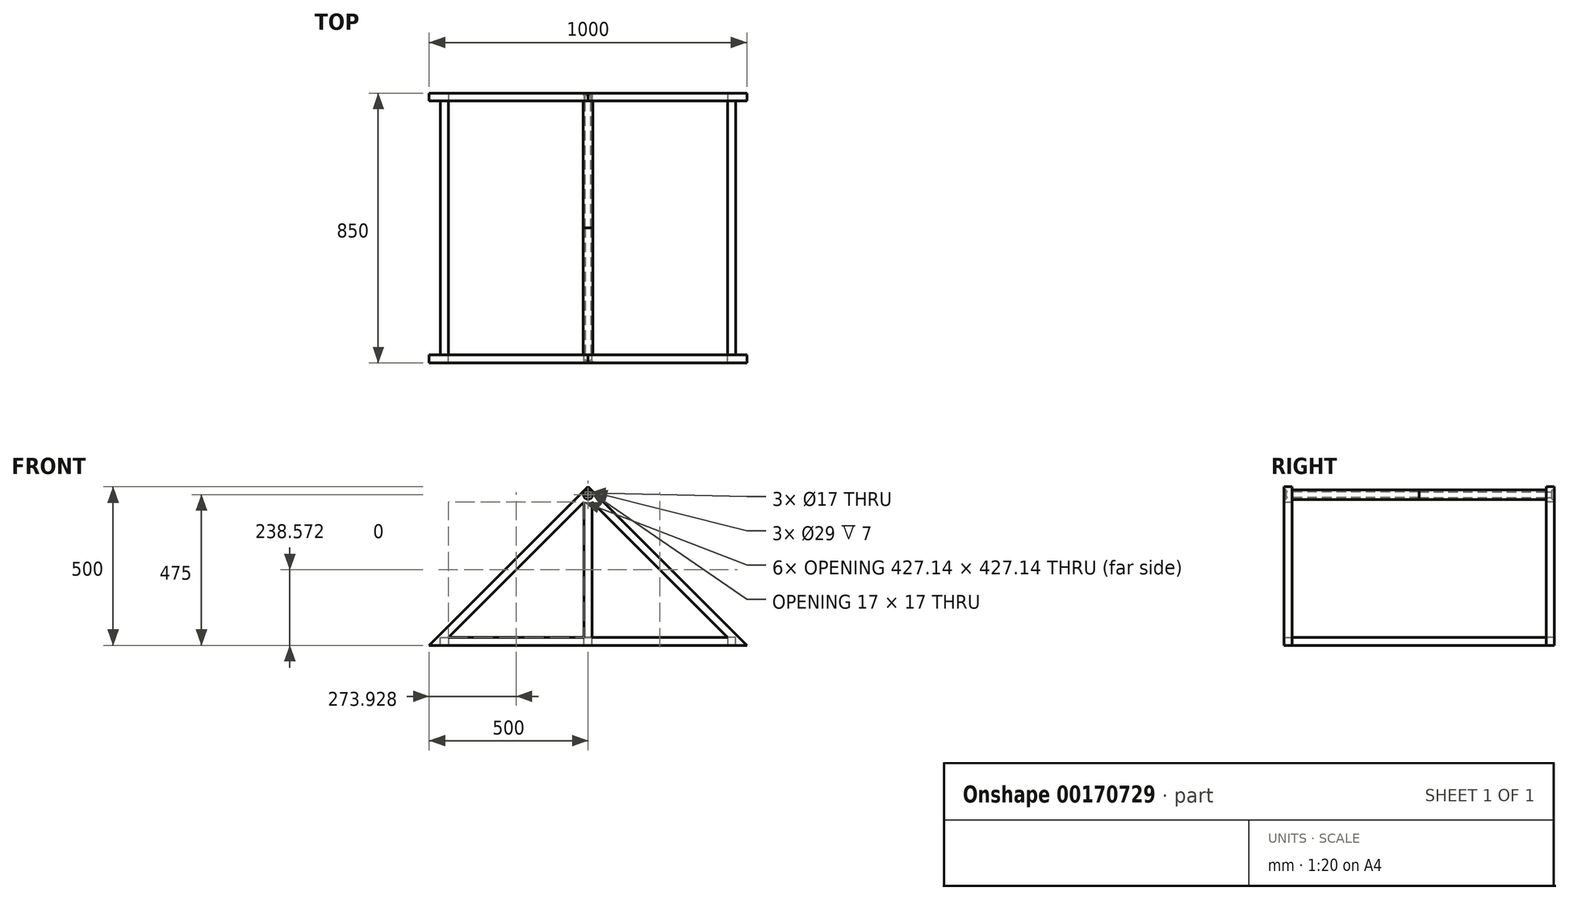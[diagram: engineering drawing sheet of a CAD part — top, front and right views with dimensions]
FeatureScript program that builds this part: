
annotation { "Feature Type Name" : "Feature", "Feature Type Description" : "" }
export const myFeature = defineFeature(function(context is Context, id is Id, definition is map)
    precondition{}
    {
        {
            var Q0;
            Q0=qCreatedBy(makeId("Front.planeOp"),FACE);
            var sketch = newSketch(context, id + "F0", { "sketchPlane" : qUnion([Q0])});
            skLineSegment(sketch, "E0", {"start": v(0, -500) * mm, "end": v(500, -500) * mm});
            skLineSegment(sketch, "E1", {"start": v(0, -500) * mm, "end": v(-500, -500) * mm});
            skLineSegment(sketch, "E2", {"start": v(0, 0) * mm, "end": v(-500, -500) * mm});
            skLineSegment(sketch, "E3", {"start": v(0, 0) * mm, "end": v(500, -500) * mm});
            skLineSegment(sketch, "E4.0", {"start": v(-12.5, -475) * mm, "end": v(-439.64, -475) * mm});
            skLineSegment(sketch, "E4.1", {"start": v(12.5, -475) * mm, "end": v(439.64, -475) * mm});
            skLineSegment(sketch, "E5.trimOffspring", {"start": v(12.5, -47.86) * mm, "end": v(12.5, -475) * mm});
            skLineSegment(sketch, "E6.trimOffspring", {"start": v(-12.5, -47.86) * mm, "end": v(-439.64, -475) * mm});
            skLineSegment(sketch, "E7.trimOffspring", {"start": v(12.5, -47.86) * mm, "end": v(439.64, -475) * mm});
            skLineSegment(sketch, "E8.trimOffspring", {"start": v(-12.5, -47.86) * mm, "end": v(-12.5, -475) * mm});
            skSolve(sketch);
        }
        {
            var Q0;
            Q0=makeQuery(id+"F0.imprint","IMPRINT",FACE,{"disambiguationData":[TD([[makeQuery(id+"F0.imprint","IMPRINT",EDGE,{"derivedFrom":sQuery(id+"F0.wireOp",EDGE,"E0")}),1.0]])]});
            extrude(context, id + "F1", {"entities" : qUnion([Q0]), "depth" : 25 * mm});
        }
        {
            var Q0;
            Q0=qCreatedBy(makeId("Front.planeOp"),FACE);
            cPlane(context, id + "F2", {"entities" : qUnion([Q0]), "cplaneType" : CPlaneType.OFFSET, "offset" : 400 * mm, "oppositeDirection" : true, "width" : 150 * mm, "height" : 150 * mm});
        }
        {
            var Q0;
            Q0=makeQuery(id+"F1.opExtrude","SWEPT_BODY",BODY,{"disambiguationData":[OSD([sQuery(id+"F0.wireOp",EDGE,"E0"),sQuery(id+"F0.wireOp",EDGE,"E1"),sQuery(id+"F0.wireOp",EDGE,"E2"),sQuery(id+"F0.wireOp",EDGE,"E3"),sQuery(id+"F0.wireOp",EDGE,"E4.0"),sQuery(id+"F0.wireOp",EDGE,"E4.1"),sQuery(id+"F0.wireOp",EDGE,"E5.trimOffspring"),sQuery(id+"F0.wireOp",EDGE,"E6.trimOffspring"),sQuery(id+"F0.wireOp",EDGE,"E7.trimOffspring"),sQuery(id+"F0.wireOp",EDGE,"E8.trimOffspring")])]});
            var Q1;
            Q1=qCreatedBy(id+"F2.planeOp",FACE);
            mirror(context, id + "F3", {"entities" : qUnion([Q0]), "mirrorPlane" : qUnion([Q1])});
        }
        {
            var Q0;
            Q0=makeQuery(id+"F1.opExtrude","CAP_FACE",FACE,{"disambiguationData":[OSD([sQuery(id+"F0.wireOp",EDGE,"E0"),sQuery(id+"F0.wireOp",EDGE,"E1"),sQuery(id+"F0.wireOp",EDGE,"E2"),sQuery(id+"F0.wireOp",EDGE,"E3"),sQuery(id+"F0.wireOp",EDGE,"E4.0"),sQuery(id+"F0.wireOp",EDGE,"E4.1"),sQuery(id+"F0.wireOp",EDGE,"E5.trimOffspring"),sQuery(id+"F0.wireOp",EDGE,"E6.trimOffspring"),sQuery(id+"F0.wireOp",EDGE,"E7.trimOffspring"),sQuery(id+"F0.wireOp",EDGE,"E8.trimOffspring")])],"isStart":true});
            var sketch = newSketch(context, id + "F4", { "sketchPlane" : qUnion([Q0])});
            skLineSegment(sketch, "E9", {"start": v(0, 0) * mm, "end": v(0, -25) * mm});
            skCircle(sketch, "E10", {"center": v(0, -25) * mm, "radius": 15 * mm});
            skCircle(sketch, "E11", {"center": v(0, -25) * mm, "radius": 8.5 * mm});
            skSolve(sketch);
        }
        {
            var Q0;
            Q0=makeQuery(id+"F3.opPattern","COPY",FACE,{"derivedFrom":makeQuery(id+"F1.opExtrude","CAP_FACE",FACE,{"disambiguationData":[OSD([sQuery(id+"F0.wireOp",EDGE,"E0"),sQuery(id+"F0.wireOp",EDGE,"E1"),sQuery(id+"F0.wireOp",EDGE,"E2"),sQuery(id+"F0.wireOp",EDGE,"E3"),sQuery(id+"F0.wireOp",EDGE,"E4.0"),sQuery(id+"F0.wireOp",EDGE,"E4.1"),sQuery(id+"F0.wireOp",EDGE,"E5.trimOffspring"),sQuery(id+"F0.wireOp",EDGE,"E6.trimOffspring"),sQuery(id+"F0.wireOp",EDGE,"E7.trimOffspring"),sQuery(id+"F0.wireOp",EDGE,"E8.trimOffspring")])],"isStart":false}),"instanceName":"1"});
            var sketch = newSketch(context, id + "F5", { "sketchPlane" : qUnion([Q0])});
            skLineSegment(sketch, "E12", {"start": v(0, 0) * mm, "end": v(0, -25) * mm});
            skCircle(sketch, "E13", {"center": v(0, -25) * mm, "radius": 14.5 * mm});
            skSolve(sketch);
        }
        {
            var Q0;
            Q0=sQuery(id+"F5.wireOp",VERTEX,"E13.center");
            var Q1;
            Q1=makeQuery(id+"F3.opPattern","COPY",BODY,{"derivedFrom":makeQuery(id+"F1.opExtrude","SWEPT_BODY",BODY,{"disambiguationData":[OSD([sQuery(id+"F0.wireOp",EDGE,"E0"),sQuery(id+"F0.wireOp",EDGE,"E1"),sQuery(id+"F0.wireOp",EDGE,"E2"),sQuery(id+"F0.wireOp",EDGE,"E3"),sQuery(id+"F0.wireOp",EDGE,"E4.0"),sQuery(id+"F0.wireOp",EDGE,"E4.1"),sQuery(id+"F0.wireOp",EDGE,"E5.trimOffspring"),sQuery(id+"F0.wireOp",EDGE,"E6.trimOffspring"),sQuery(id+"F0.wireOp",EDGE,"E7.trimOffspring"),sQuery(id+"F0.wireOp",EDGE,"E8.trimOffspring")])]}),"instanceName":"1"});
            hole(context, id + "F6", {"style" : HoleStyle.C_BORE, "endStyle" : HoleEndStyle.BLIND, "holeDiameter" : 17 * mm, "cBoreDiameter" : 29 * mm, "cBoreDepth" : 7 * mm, "holeDepth" : 100 * mm, "locations" : qUnion([Q0]), "scope" : qUnion([Q1])});
        }
        {
            var Q0;
            Q0=makeQuery(id+"F1.opExtrude","CAP_FACE",FACE,{"disambiguationData":[OSD([sQuery(id+"F0.wireOp",EDGE,"E0"),sQuery(id+"F0.wireOp",EDGE,"E1"),sQuery(id+"F0.wireOp",EDGE,"E2"),sQuery(id+"F0.wireOp",EDGE,"E3"),sQuery(id+"F0.wireOp",EDGE,"E4.0"),sQuery(id+"F0.wireOp",EDGE,"E4.1"),sQuery(id+"F0.wireOp",EDGE,"E5.trimOffspring"),sQuery(id+"F0.wireOp",EDGE,"E6.trimOffspring"),sQuery(id+"F0.wireOp",EDGE,"E7.trimOffspring"),sQuery(id+"F0.wireOp",EDGE,"E8.trimOffspring")])],"isStart":false});
            var sketch = newSketch(context, id + "F7", { "sketchPlane" : qUnion([Q0])});
            skLineSegment(sketch, "E14", {"start": v(0, 0) * mm, "end": v(0, -25) * mm});
            skSolve(sketch);
        }
        {
            var Q0;
            Q0=sQuery(id+"F7.wireOp",VERTEX,"E14.end");
            var Q1;
            Q1=makeQuery(id+"F1.opExtrude","SWEPT_BODY",BODY,{"disambiguationData":[OSD([sQuery(id+"F0.wireOp",EDGE,"E0"),sQuery(id+"F0.wireOp",EDGE,"E1"),sQuery(id+"F0.wireOp",EDGE,"E2"),sQuery(id+"F0.wireOp",EDGE,"E3"),sQuery(id+"F0.wireOp",EDGE,"E4.0"),sQuery(id+"F0.wireOp",EDGE,"E4.1"),sQuery(id+"F0.wireOp",EDGE,"E5.trimOffspring"),sQuery(id+"F0.wireOp",EDGE,"E6.trimOffspring"),sQuery(id+"F0.wireOp",EDGE,"E7.trimOffspring"),sQuery(id+"F0.wireOp",EDGE,"E8.trimOffspring")])]});
            hole(context, id + "F8", {"style" : HoleStyle.C_BORE, "endStyle" : HoleEndStyle.BLIND, "holeDiameter" : 17 * mm, "cBoreDiameter" : 29 * mm, "cBoreDepth" : 7 * mm, "holeDepth" : 100 * mm, "locations" : qUnion([Q0]), "scope" : qUnion([Q1])});
        }
        {
            var Q0;
            Q0=makeQuery(id+"F4.imprint","IMPRINT",FACE,{"disambiguationData":[TD([[makeQuery(id+"F4.imprint","IMPRINT",EDGE,{"derivedFrom":sQuery(id+"F4.wireOp",EDGE,"E10")}),1.0]])]});
            extrude(context, id + "F9", {"entities" : qUnion([Q0]), "operationType" : NewBodyOperationType.ADD, "depth" : 400 * mm});
        }
        {
            var Q0;
            Q0=makeQuery(id+"F1.opExtrude","SWEPT_BODY",BODY,{"disambiguationData":[OSD([sQuery(id+"F0.wireOp",EDGE,"E0"),sQuery(id+"F0.wireOp",EDGE,"E1"),sQuery(id+"F0.wireOp",EDGE,"E2"),sQuery(id+"F0.wireOp",EDGE,"E3"),sQuery(id+"F0.wireOp",EDGE,"E4.0"),sQuery(id+"F0.wireOp",EDGE,"E4.1"),sQuery(id+"F0.wireOp",EDGE,"E5.trimOffspring"),sQuery(id+"F0.wireOp",EDGE,"E6.trimOffspring"),sQuery(id+"F0.wireOp",EDGE,"E7.trimOffspring"),sQuery(id+"F0.wireOp",EDGE,"E8.trimOffspring")])]});
            var Q1;
            Q1=qCreatedBy(id+"F2.planeOp",FACE);
            mirror(context, id + "F10", {"entities" : qUnion([Q0]), "mirrorPlane" : qUnion([Q1])});
        }
        {
            var Q0;
            Q0=makeQuery(id+"F10.opPattern","COPY",FACE,{"derivedFrom":makeQuery(id+"F1.opExtrude","SWEPT_FACE",FACE,{"disambiguationData":[OSD([sQuery(id+"F0.wireOp",EDGE,"E4.0")])]}),"instanceName":"1"});
            var sketch = newSketch(context, id + "F11", { "sketchPlane" : qUnion([Q0])});
            skLineSegment(sketch, "E15", {"start": v(-12.5, 825) * mm, "end": v(-12.5, -24.65) * mm});
            skLineSegment(sketch, "E16", {"start": v(12.93, -25.06) * mm, "end": v(12.45, 824.95) * mm});
            skLineSegment(sketch, "E17", {"start": v(-12.5, 800) * mm, "end": v(12.46, 800) * mm});
            skLineSegment(sketch, "E18", {"start": v(12.92, 0) * mm, "end": v(-12.5, 0) * mm});
            skSolve(sketch);
        }
        {
            var Q0;
            Q0 = qSketchRegion(id + "F11", true);
            extrude(context, id + "F12", {"entities" : qUnion([Q0]), "oppositeDirection" : true, "depth" : 25 * mm});
        }
        {
            var Q0;
            Q0=makeQuery(id+"F3.opPattern","COPY",FACE,{"derivedFrom":makeQuery(id+"F1.opExtrude","CAP_FACE",FACE,{"disambiguationData":[OSD([sQuery(id+"F0.wireOp",EDGE,"E0"),sQuery(id+"F0.wireOp",EDGE,"E1"),sQuery(id+"F0.wireOp",EDGE,"E2"),sQuery(id+"F0.wireOp",EDGE,"E3"),sQuery(id+"F0.wireOp",EDGE,"E4.0"),sQuery(id+"F0.wireOp",EDGE,"E4.1"),sQuery(id+"F0.wireOp",EDGE,"E5.trimOffspring"),sQuery(id+"F0.wireOp",EDGE,"E6.trimOffspring"),sQuery(id+"F0.wireOp",EDGE,"E7.trimOffspring"),sQuery(id+"F0.wireOp",EDGE,"E8.trimOffspring")])],"isStart":true}),"instanceName":"1"});
            var sketch = newSketch(context, id + "F13", { "sketchPlane" : qUnion([Q0])});
            skLineSegment(sketch, "E19", {"start": v(439.64, -475) * mm, "end": v(439.64, -500) * mm});
            skLineSegment(sketch, "E20", {"start": v(439.64, -500) * mm, "end": v(464.64, -500) * mm});
            skLineSegment(sketch, "E21", {"start": v(464.64, -500) * mm, "end": v(464.64, -475) * mm});
            skLineSegment(sketch, "E22", {"start": v(464.64, -475) * mm, "end": v(439.64, -475) * mm});
            skSolve(sketch);
        }
        {
            var Q0;
            Q0 = qSketchRegion(id + "F13", true);
            extrude(context, id + "F14", {"entities" : qUnion([Q0]), "depth" : 800 * mm});
        }
        {
            var Q0;
            Q0=makeQuery(id+"F1.opExtrude","CAP_FACE",FACE,{"disambiguationData":[OSD([sQuery(id+"F0.wireOp",EDGE,"E0"),sQuery(id+"F0.wireOp",EDGE,"E1"),sQuery(id+"F0.wireOp",EDGE,"E2"),sQuery(id+"F0.wireOp",EDGE,"E3"),sQuery(id+"F0.wireOp",EDGE,"E4.0"),sQuery(id+"F0.wireOp",EDGE,"E4.1"),sQuery(id+"F0.wireOp",EDGE,"E5.trimOffspring"),sQuery(id+"F0.wireOp",EDGE,"E6.trimOffspring"),sQuery(id+"F0.wireOp",EDGE,"E7.trimOffspring"),sQuery(id+"F0.wireOp",EDGE,"E8.trimOffspring")])],"isStart":true});
            var sketch = newSketch(context, id + "F15", { "sketchPlane" : qUnion([Q0])});
            skLineSegment(sketch, "E23", {"start": v(439.64, -475) * mm, "end": v(439.64, -500) * mm});
            skLineSegment(sketch, "E24", {"start": v(439.64, -500) * mm, "end": v(464.64, -500) * mm});
            skLineSegment(sketch, "E25", {"start": v(464.64, -500) * mm, "end": v(464.64, -475) * mm});
            skLineSegment(sketch, "E26", {"start": v(464.64, -475) * mm, "end": v(439.64, -475) * mm});
            skSolve(sketch);
        }
        {
            var Q0;
            Q0 = qSketchRegion(id + "F15", true);
            extrude(context, id + "F16", {"entities" : qUnion([Q0]), "depth" : 800 * mm});
        }
    });
